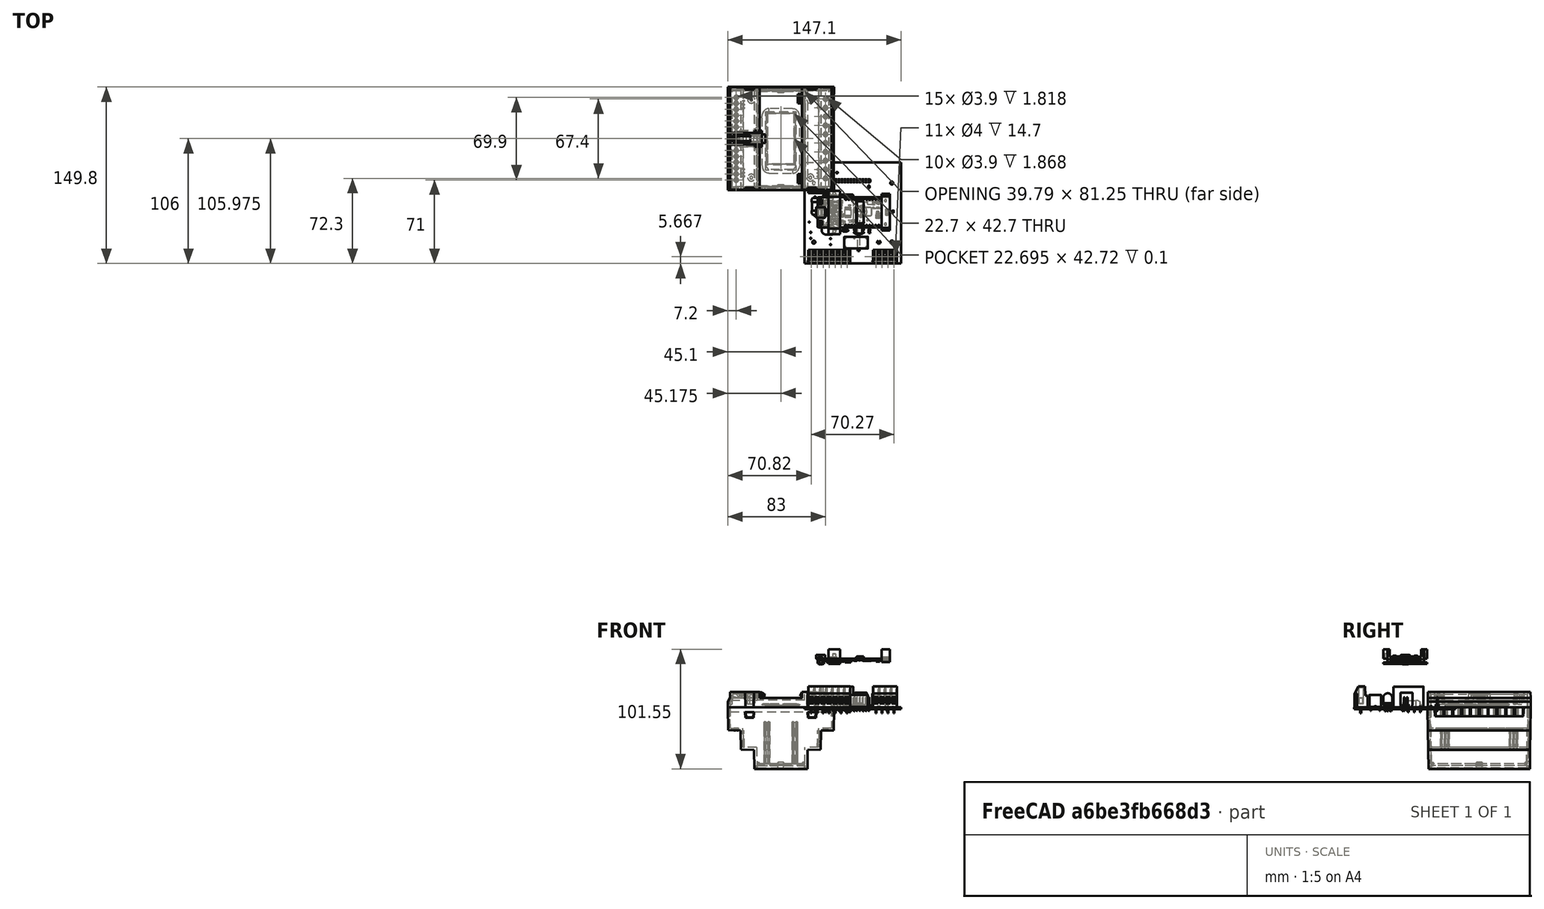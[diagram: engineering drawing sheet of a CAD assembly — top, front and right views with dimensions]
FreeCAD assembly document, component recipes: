
FREECAD ASSEMBLY — COMPONENT RECIPES ("heating-controller-integration")

This assembly document has 6 components, labeled P0..P5 below (a component is one placed body or linked part). 3 of them carry a construction recipe — the FreeCAD feature program that regenerates the part from scratch, quoted from this document or its linked companion documents; the rest are supplied as boundary geometry only. No exploded tour is included for this assembly.
COMPONENT P0 — geometry summary ("heating-controller"; no construction recipe available for this part):
  bounding box: 85.9 x 81.9 x 23.0 mm
  tessellated surface: 121,010 triangles
  volume: 35747 mm^3 (22% of its bounding box)
COMPONENT P1 — recipe-attached ("Support_antenna", modeled in this document).
Construction recipe (the document's own serialized feature program — sketch geometry with constraints, then the solid features built on it; lengths are millimeters unless a unit is written):

FEATURE [Sketcher::SketchObject] Sketch002
  FullyConstrained = true
  MapMode = 5
  Placement = pos=(0,0,0) rot=(0.57735,0.57735,0.57735;2.0944rad)
  Support = -> [YZ_Plane013]
  sketch-geometry (12):
    g0: LineSegment StartX=0 StartY=0 StartZ=0 EndX=2 EndY=0 EndZ=0
    g1: LineSegment StartX=2 StartY=0 StartZ=0 EndX=2 EndY=-6.5 EndZ=0
    g2: LineSegment StartX=2 StartY=-6.5 StartZ=0 EndX=29 EndY=-6.5 EndZ=0
    g3: LineSegment StartX=29 StartY=-6.5 StartZ=0 EndX=29 EndY=0 EndZ=0
    g4: LineSegment StartX=29 StartY=0 StartZ=0 EndX=31 EndY=0 EndZ=0
    g5: LineSegment StartX=31 StartY=0 StartZ=0 EndX=31 EndY=-10.8 EndZ=0
    g6: LineSegment StartX=31 StartY=-10.8 StartZ=0 EndX=0 EndY=-10.8 EndZ=0
    g7: LineSegment StartX=0 StartY=-10.8 StartZ=0 EndX=0 EndY=0 EndZ=0
    g8: LineSegment StartX=2 StartY=-8 StartZ=0 EndX=29 EndY=-8 EndZ=0
    g9: LineSegment StartX=29 StartY=-8 StartZ=0 EndX=29 EndY=-9.3 EndZ=0
    g10: LineSegment StartX=29 StartY=-9.3 StartZ=0 EndX=2 EndY=-9.3 EndZ=0
    g11: LineSegment StartX=2 StartY=-9.3 StartZ=0 EndX=2 EndY=-8 EndZ=0
  constraints (35):
    c: Coincident(g-1,g0)
    c: PointOnObject(g0,g-1)
    c: Coincident(g0,g1)
    c: Vertical(g1)
    c: Coincident(g1,g2)
    c: Horizontal(g2)
    c: Coincident(g2,g3)
    c: PointOnObject(g3,g-1)
    c: Vertical(g3)
    c: Coincident(g3,g4)
    c: PointOnObject(g4,g-1)
    c: Coincident(g4,g5)
    c: Vertical(g5)
    c: Coincident(g5,g6)
    c: PointOnObject(g6,g-2)
    c: Horizontal(g6)
    c: Coincident(g6,g7)
    c: Coincident(g7,g0)
    c: Equal(g0,g4)
    c: DistanceX(g0,g0) = 2
    c: DistanceX(g2,g2) = 27
    c: DistanceY(g3,g3) = 6.5
    c: Coincident(g8,g9)
    c: Coincident(g9,g10)
    c: Coincident(g10,g11)
    c: Coincident(g11,g8)
    c: Horizontal(g8)
    c: Horizontal(g10)
    c: Vertical(g9)
    c: Vertical(g11)
    c: Vertical(g8,g2)
    c: Vertical(g8,g1)
    c: DistanceY(g9,g9) = 1.3
    c: DistanceY(g6,g10) = 1.5
    c: DistanceY(g8,g1) = 1.5
FEATURE [PartDesign::Pad] Pad
  Direction = (1,-2e-16,3e-16)
  Length = 7
  Length2 = 10
  Placement = pos=(0,0,0) rot=(0.57735,0.57735,0.57735;2.0944rad)
  Profile = -> Sketch002
  ReferenceAxis = -> Sketch002 [N_Axis]
  Type = 0
FEATURE [PartDesign::Body] Body  label="Support_antenna"
  Group = -> [Sketch002,Pad]
  Origin = -> Origin013
  Placement = pos=(85.4,-77.9,49.4) rot=(0,0,1;0rad)
  Tip = -> Pad
COMPONENT P2 — recipe-attached ("Support_PCB", modeled in this document).
Construction recipe (the document's own serialized feature program — sketch geometry with constraints, then the solid features built on it; lengths are millimeters unless a unit is written):

FEATURE [Sketcher::SketchObject] Sketch003
  FullyConstrained = true
  MapMode = 5
  Placement = pos=(0,0,0) rot=(0.57735,0.57735,0.57735;2.0944rad)
  Support = -> [YZ_Plane014]
  sketch-geometry (8):
    g0: LineSegment StartX=0 StartY=0 StartZ=0 EndX=5 EndY=0 EndZ=0
    g1: LineSegment StartX=5 StartY=0 StartZ=0 EndX=5 EndY=-6.5 EndZ=0
    g2: LineSegment StartX=5 StartY=-6.5 StartZ=0 EndX=32 EndY=-6.5 EndZ=0
    g3: LineSegment StartX=32 StartY=-6.5 StartZ=0 EndX=32 EndY=0 EndZ=0
    g4: LineSegment StartX=32 StartY=0 StartZ=0 EndX=37 EndY=0 EndZ=0
    g5: LineSegment StartX=37 StartY=0 StartZ=0 EndX=37 EndY=-8 EndZ=0
    g6: LineSegment StartX=37 StartY=-8 StartZ=0 EndX=0 EndY=-8 EndZ=0
    g7: LineSegment StartX=0 StartY=-8 StartZ=0 EndX=0 EndY=0 EndZ=0
  constraints (23):
    c: Coincident(g-1,g0)
    c: PointOnObject(g0,g-1)
    c: Coincident(g0,g1)
    c: Vertical(g1)
    c: Coincident(g1,g2)
    c: Horizontal(g2)
    c: Coincident(g2,g3)
    c: PointOnObject(g3,g-1)
    c: Vertical(g3)
    c: Coincident(g3,g4)
    c: PointOnObject(g4,g-1)
    c: Coincident(g4,g5)
    c: Vertical(g5)
    c: Coincident(g5,g6)
    c: PointOnObject(g6,g-2)
    c: Horizontal(g6)
    c: Coincident(g6,g7)
    c: Coincident(g7,g0)
    c: Equal(g0,g4)
    c: DistanceX(g0,g0) = 5
    c: DistanceX(g2,g2) = 27
    c: DistanceY(g3,g3) = 6.5
    c: DistanceY(g6,g1) = 1.5
FEATURE [PartDesign::Pad] Pad001
  Direction = (1,-2e-16,3e-16)
  Length = 10
  Length2 = 10
  Placement = pos=(0,0,0) rot=(0.57735,0.57735,0.57735;2.0944rad)
  Profile = -> Sketch003
  ReferenceAxis = -> Sketch003 [N_Axis]
  Type = 0
FEATURE [Sketcher::SketchObject] Sketch004
  ExternalGeometry = -> [Pad001]
  FullyConstrained = true
  MapMode = 5
  Placement = pos=(3.1e-15,-4.4e-15,-8) rot=(0.707107,0.707107,0;3.14159rad)
  Support = -> [Pad001]
  sketch-geometry (4):
    g0: Circle CenterX=2.5 CenterY=5 CenterZ=0 NormalX=0 NormalY=0 NormalZ=1 AngleXU=0 Radius=1.25
    g1: Circle CenterX=34.5 CenterY=5 CenterZ=0 NormalX=0 NormalY=0 NormalZ=1 AngleXU=0 Radius=1.25
    g2: LineSegment StartX=34.5 StartY=5 StartZ=0 EndX=37 EndY=9e-16 EndZ=0
    g3: LineSegment StartX=34.5 StartY=5 StartZ=0 EndX=37 EndY=10 EndZ=0
  constraints (10):
    c: Horizontal(g0,g1)
    c: Equal(g0,g1)
    c: Diameter(g0) = 2.5
    c: DistanceX(g-1,g0) = 2.5
    c: DistanceX(g1,g-3) = 2.5
    c: Coincident(g2,g1)
    c: Coincident(g2,g-3)
    c: Coincident(g3,g1)
    c: Coincident(g3,g-3)
    c: Equal(g3,g2)
FEATURE [PartDesign::Pocket] Pocket
  BaseFeature = -> Pad001
  Direction = (-4e-16,6e-16,1)
  Length = 4
  Length2 = 5
  Placement = pos=(0,0,0) rot=(0.57735,0.57735,0.57735;2.0944rad)
  Profile = -> Sketch004
  ReferenceAxis = -> Sketch004 [N_Axis]
  Type = 0
FEATURE [PartDesign::Body] Body001  label="Support_PCB"
  Group = -> [Sketch003,Pad001,Sketch004,Pocket]
  Origin = -> Origin014
  Placement = pos=(40.3,-81.25,49.4) rot=(0,0,1;0rad)
  Tip = -> Pocket
COMPONENT P3 — recipe-attached ("Support_PCB_top", modeled in this document).
Construction recipe (the document's own serialized feature program — sketch geometry with constraints, then the solid features built on it; lengths are millimeters unless a unit is written):

FEATURE [Sketcher::SketchObject] Sketch005
  FullyConstrained = true
  MapMode = 5
  Placement = pos=(0,0,0) rot=(0.57735,0.57735,0.57735;2.0944rad)
  Support = -> [YZ_Plane015]
  sketch-geometry (6):
    g0: LineSegment StartX=0 StartY=0 StartZ=0 EndX=5 EndY=0 EndZ=0
    g1: LineSegment StartX=5 StartY=0 StartZ=0 EndX=32 EndY=0 EndZ=0
    g2: LineSegment StartX=32 StartY=0 StartZ=0 EndX=37 EndY=0 EndZ=0
    g3: LineSegment StartX=37 StartY=0 StartZ=0 EndX=37 EndY=-1.5 EndZ=0
    g4: LineSegment StartX=37 StartY=-1.5 StartZ=0 EndX=0 EndY=-1.5 EndZ=0
    g5: LineSegment StartX=0 StartY=-1.5 StartZ=0 EndX=0 EndY=0 EndZ=0
  constraints (17):
    c: Coincident(g-1,g0)
    c: PointOnObject(g0,g-1)
    c: Horizontal(g1)
    c: PointOnObject(g2,g-1)
    c: Coincident(g2,g3)
    c: Vertical(g3)
    c: Coincident(g3,g4)
    c: PointOnObject(g4,g-2)
    c: Horizontal(g4)
    c: Coincident(g4,g5)
    c: Coincident(g5,g0)
    c: Equal(g0,g2)
    c: DistanceX(g0,g0) = 5
    c: DistanceX(g1,g1) = 27
    c: DistanceY(g4,g1) = 1.5
    c: Coincident(g1,g2)
    c: Coincident(g0,g1)
FEATURE [PartDesign::Pad] Pad002
  Direction = (1,-2e-16,3e-16)
  Length = 10
  Length2 = 10
  Placement = pos=(0,0,0) rot=(0.57735,0.57735,0.57735;2.0944rad)
  Profile = -> Sketch005
  ReferenceAxis = -> Sketch005 [N_Axis]
  Type = 0
FEATURE [Sketcher::SketchObject] Sketch006
  ExternalGeometry = -> [Pad002]
  FullyConstrained = true
  MapMode = 5
  Placement = pos=(6e-16,-8e-16,-1.5) rot=(0.707107,0.707107,0;3.14159rad)
  Support = -> [Pad002]
  sketch-geometry (4):
    g0: Circle CenterX=2.5 CenterY=5 CenterZ=0 NormalX=0 NormalY=0 NormalZ=1 AngleXU=0 Radius=1.4
    g1: Circle CenterX=34.5 CenterY=5 CenterZ=0 NormalX=0 NormalY=0 NormalZ=1 AngleXU=0 Radius=1.4
    g2: LineSegment StartX=34.5 StartY=5 StartZ=0 EndX=37 EndY=0 EndZ=0
    g3: LineSegment StartX=34.5 StartY=5 StartZ=0 EndX=37 EndY=10 EndZ=0
  constraints (10):
    c: Horizontal(g0,g1)
    c: Equal(g0,g1)
    c: Diameter(g0) = 2.8
    c: DistanceX(g-1,g0) = 2.5
    c: DistanceX(g1,g-3) = 2.5
    c: Coincident(g2,g1)
    c: Coincident(g2,g-3)
    c: Coincident(g3,g1)
    c: Coincident(g3,g-3)
    c: Equal(g3,g2)
FEATURE [PartDesign::Pocket] Pocket001
  BaseFeature = -> Pad002
  Direction = (-4e-16,6e-16,1)
  Length = 5
  Length2 = 5
  Placement = pos=(0,0,0) rot=(0.57735,0.57735,0.57735;2.0944rad)
  Profile = -> Sketch006
  ReferenceAxis = -> Sketch006 [N_Axis]
  Type = 1
FEATURE [PartDesign::Body] Body002  label="Support_PCB_top"
  Group = -> [Sketch005,Pad002,Sketch006,Pocket001]
  Origin = -> Origin015
  Placement = pos=(40.3,-81.25,38.35) rot=(0,0,1;0rad)
  Tip = -> Pocket001
COMPONENT P4 — geometry summary ("S-WATCH_20220510_ASM_ASM_1_ASM__ASM"; no construction recipe available for this part):
  bounding box: 55.0 x 32.0 x 2.9 mm
  tessellated surface: 19,934 triangles
  volume: 3631 mm^3 (70% of its bounding box)
  symmetry: mirror-symmetric across its y mid-plane
COMPONENT P5 — geometry summary ("enclosure"; no construction recipe available for this part):
  bounding box: 90.2 x 87.6 x 65.4 mm
  tessellated surface: 29,414 triangles
  volume: 71583 mm^3 (14% of its bounding box)
  symmetry: mirror-symmetric across its x mid-plane
PROVENANCE & LICENSES
A FreeCAD (.FCStd) document from a public repository crawl; recipes are the document's own serialized feature recipes (and, for linked parts, companion documents' recipes).
License: as declared in the source repository (recorded in the dataset sidecar).
